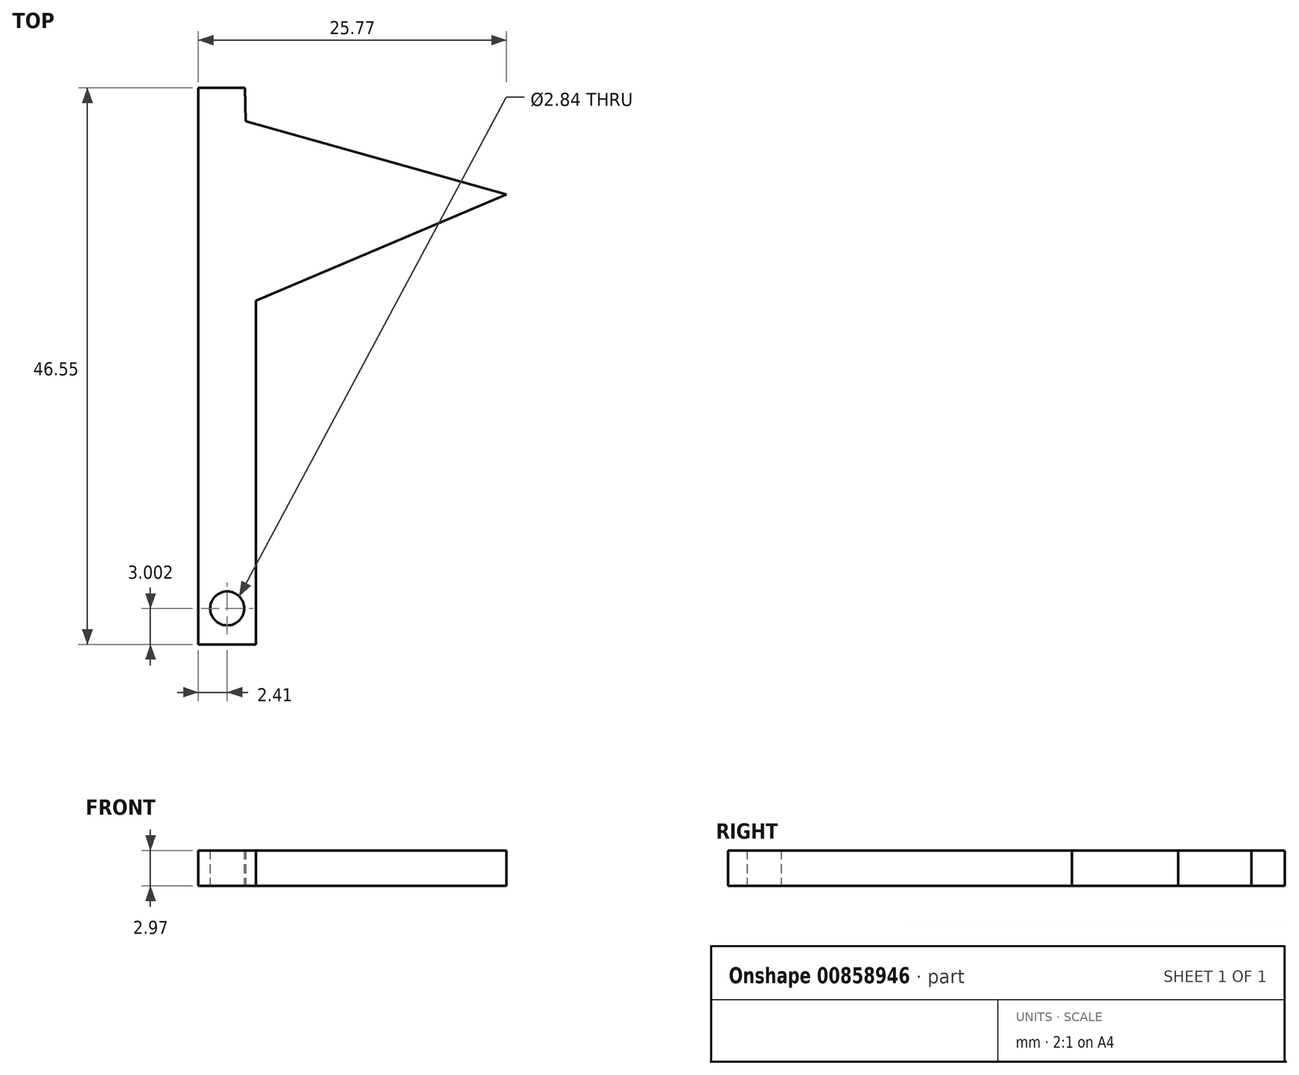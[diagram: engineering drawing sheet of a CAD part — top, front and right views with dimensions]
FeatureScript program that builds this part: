
annotation { "Feature Type Name" : "Feature", "Feature Type Description" : "" }
export const myFeature = defineFeature(function(context is Context, id is Id, definition is map)
    precondition{}
    {
        {
            var Q0;
            Q0=qCreatedBy(makeId("Top.planeOp"),FACE);
            var sketch = newSketch(context, id + "F0", { "sketchPlane" : qUnion([Q0])});
            skLineSegment(sketch, "E0", {"start": v(10.37, -4.38) * mm, "end": v(10.37, 24.38) * mm});
            skLineSegment(sketch, "E1", {"start": v(10.37, 24.38) * mm, "end": v(31.32, 33.27) * mm});
            skLineSegment(sketch, "E2", {"start": v(31.32, 33.27) * mm, "end": v(9.52, 39.4) * mm});
            skLineSegment(sketch, "E3", {"start": v(5.55, 39.4) * mm, "end": v(5.55, -4.38) * mm});
            skLineSegment(sketch, "E4", {"start": v(5.55, -4.38) * mm, "end": v(10.37, -4.38) * mm});
            skCircle(sketch, "E5", {"center": v(7.96, -1.38) * mm, "radius": 1.42 * mm});
            skPoint(sketch, "E5.centerSnap0", {"position": v(7.96, -4.38) * mm});
            skLineSegment(sketch, "E6", {"start": v(5.55, 39.4) * mm, "end": v(5.55, 42.17) * mm});
            skLineSegment(sketch, "E7", {"start": v(5.55, 42.17) * mm, "end": v(9.46, 42.17) * mm});
            skLineSegment(sketch, "E8", {"start": v(9.46, 42.17) * mm, "end": v(9.52, 39.4) * mm});
            skSolve(sketch);
        }
        {
            var Q0;
            Q0=makeQuery(id+"F0.imprint","IMPRINT",FACE,{"disambiguationData":[TD([[makeQuery(id+"F0.imprint","IMPRINT",EDGE,{"derivedFrom":sQuery(id+"F0.wireOp",EDGE,"E0")}),1.0]])]});
            extrude(context, id + "F1", {"entities" : qUnion([Q0]), "depth" : 2.97 * mm, "offsetDistance" : 25.4 * mm});
        }
    });
